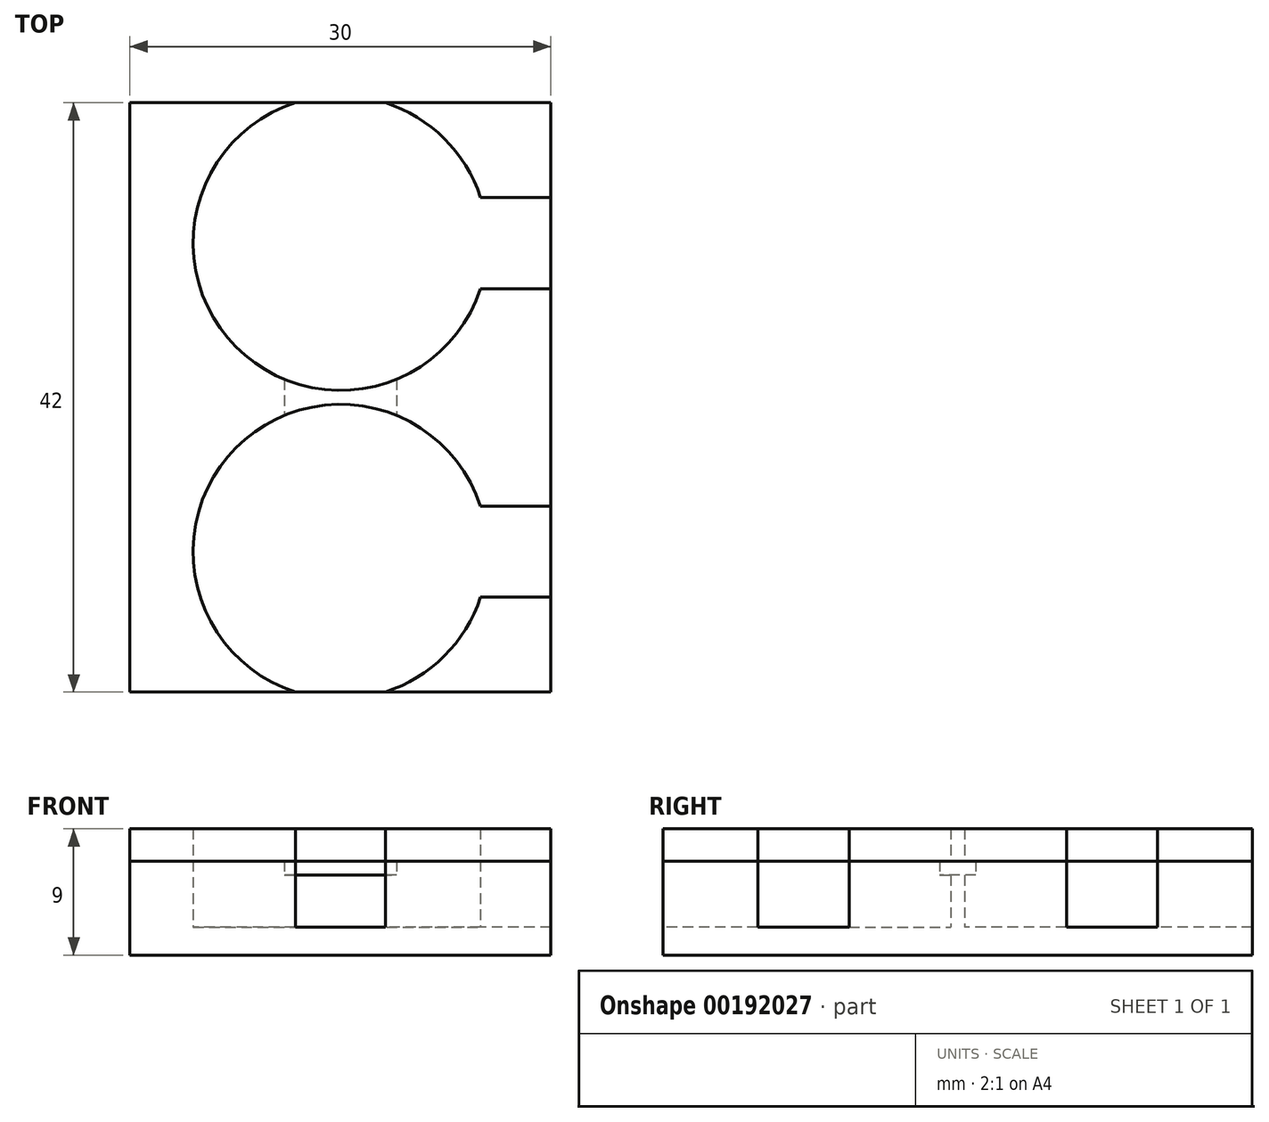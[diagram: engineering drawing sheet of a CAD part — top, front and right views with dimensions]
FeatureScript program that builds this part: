
annotation { "Feature Type Name" : "Feature", "Feature Type Description" : "" }
export const myFeature = defineFeature(function(context is Context, id is Id, definition is map)
    precondition{}
    {
        {
            var Q0;
            Q0=qCreatedBy(makeId("Top.planeOp"),FACE);
            var sketch = newSketch(context, id + "F0", { "sketchPlane" : qUnion([Q0])});
            skLineSegment(sketch, "E0.bottom", {"start": v(-15, 21) * mm, "end": v(15, 21) * mm});
            skLineSegment(sketch, "E0.top", {"start": v(-15, -21) * mm, "end": v(15, -21) * mm});
            skLineSegment(sketch, "E0.left", {"start": v(-15, 21) * mm, "end": v(-15, -21) * mm});
            skLineSegment(sketch, "E0.right", {"start": v(15, 21) * mm, "end": v(15, -21) * mm});
            skPoint(sketch, "E0.middle", {"position": v(0, 0) * mm});
            skSolve(sketch);
        }
        {
            var Q0;
            Q0=makeQuery(id+"F0.imprint","IMPRINT",FACE,{"disambiguationData":[TD([[makeQuery(id+"F0.imprint","IMPRINT",EDGE,{"derivedFrom":sQuery(id+"F0.wireOp",EDGE,"E0.bottom")}),-1.0]])]});
            var sketch = newSketch(context, id + "F1", { "sketchPlane" : qUnion([Q0])});
            skCircle(sketch, "E1", {"center": v(0, 11) * mm, "radius": 10.5 * mm});
            skSolve(sketch);
        }
        {
            var Q0;
            Q0=makeQuery(id+"F1.imprint","IMPRINT",FACE,{"disambiguationData":[TD([[makeQuery(id+"F1.imprint","IMPRINT",EDGE,{"derivedFrom":sQuery(id+"F1.wireOp",EDGE,"E1")}),-1.0]])]});
            var sketch = newSketch(context, id + "F2", { "sketchPlane" : qUnion([Q0])});
            skCircle(sketch, "E2", {"center": v(0, -11) * mm, "radius": 10.5 * mm});
            skSolve(sketch);
        }
        {
            var Q0;
            Q0=makeQuery(id+"F0.imprint","IMPRINT",FACE,{"disambiguationData":[TD([[makeQuery(id+"F0.imprint","IMPRINT",EDGE,{"derivedFrom":sQuery(id+"F0.wireOp",EDGE,"E0.bottom")}),-1.0]])]});
            extrude(context, id + "F3", {"entities" : qUnion([Q0]), "oppositeDirection" : true, "depth" : 2 * mm});
        }
        {
            var Q0;
            Q0=makeQuery(id+"F2.imprint","IMPRINT",FACE,{"disambiguationData":[TD([[makeQuery(id+"F2.imprint","IMPRINT",EDGE,{"derivedFrom":sQuery(id+"F2.wireOp",EDGE,"E2")}),-1.0]])]});
            var sketch = newSketch(context, id + "F4", { "sketchPlane" : qUnion([Q0])});
            skLineSegment(sketch, "E3.bottom", {"start": v(-0.01, -14.25) * mm, "end": v(17.7, -14.25) * mm});
            skLineSegment(sketch, "E3.top", {"start": v(-0.01, -7.75) * mm, "end": v(17.7, -7.75) * mm});
            skLineSegment(sketch, "E3.left", {"start": v(-0.01, -14.25) * mm, "end": v(-0.01, -7.75) * mm});
            skLineSegment(sketch, "E3.right", {"start": v(17.7, -14.25) * mm, "end": v(17.7, -7.75) * mm});
            skPoint(sketch, "E3.middle", {"position": v(0.75, 0) * mm});
            skSolve(sketch);
        }
        {
            var Q0;
            Q0=makeQuery(id+"F2.imprint","IMPRINT",FACE,{"disambiguationData":[TD([[makeQuery(id+"F2.imprint","IMPRINT",EDGE,{"derivedFrom":sQuery(id+"F2.wireOp",EDGE,"E2")}),-1.0]])]});
            var sketch = newSketch(context, id + "F5", { "sketchPlane" : qUnion([Q0])});
            skLineSegment(sketch, "E4.bottom", {"start": v(18, 14.25) * mm, "end": v(0, 14.25) * mm});
            skLineSegment(sketch, "E4.top", {"start": v(18, 7.75) * mm, "end": v(0, 7.75) * mm});
            skLineSegment(sketch, "E4.left", {"start": v(18, 14.25) * mm, "end": v(18, 7.75) * mm});
            skLineSegment(sketch, "E4.right", {"start": v(0, 14.25) * mm, "end": v(0, 7.75) * mm});
            skPoint(sketch, "E4.middle", {"position": v(0, 0) * mm});
            skSolve(sketch);
        }
        {
            var Q0;
            Q0 = qSketchRegion(id + "F0", true);
            extrude(context, id + "F6", {"entities" : qUnion([Q0]), "operationType" : NewBodyOperationType.ADD, "depth" : 4.7 * mm});
        }
        {
            var Q0;
            Q0=makeQuery(id+"F6.opExtrude","CAP_FACE",FACE,{"disambiguationData":[OSD([sQuery(id+"F0.wireOp",EDGE,"E0.bottom"),sQuery(id+"F0.wireOp",EDGE,"E0.top"),sQuery(id+"F0.wireOp",EDGE,"E0.left"),sQuery(id+"F0.wireOp",EDGE,"E0.right")])],"isStart":false});
            extrude(context, id + "F7", {"entities" : qUnion([Q0]), "depth" : 2.3 * mm});
        }
        {
            var Q0;
            Q0 = qSketchRegion(id + "F1", true);
            extrude(context, id + "F8", {"entities" : qUnion([Q0]), "operationType" : NewBodyOperationType.REMOVE, "depth" : 25 * mm});
        }
        {
            var Q0;
            Q0 = qSketchRegion(id + "F2", true);
            extrude(context, id + "F9", {"entities" : qUnion([Q0]), "operationType" : NewBodyOperationType.REMOVE, "depth" : 25 * mm});
        }
        {
            var Q0;
            Q0 = qSketchRegion(id + "F4", true);
            extrude(context, id + "F10", {"entities" : qUnion([Q0]), "operationType" : NewBodyOperationType.REMOVE, "depth" : 25 * mm});
        }
        {
            var Q0;
            Q0 = qSketchRegion(id + "F5", true);
            extrude(context, id + "F11", {"entities" : qUnion([Q0]), "operationType" : NewBodyOperationType.REMOVE, "depth" : 25 * mm});
        }
        {
            var Q0;
            Q0=makeQuery(id+"F6.opExtrude","CAP_FACE",FACE,{"disambiguationData":[OSD([sQuery(id+"F0.wireOp",EDGE,"E0.bottom"),sQuery(id+"F0.wireOp",EDGE,"E0.top"),sQuery(id+"F0.wireOp",EDGE,"E0.left"),sQuery(id+"F0.wireOp",EDGE,"E0.right")])],"isStart":false});
            var sketch = newSketch(context, id + "F12", { "sketchPlane" : qUnion([Q0])});
            skLineSegment(sketch, "E5.bottom", {"start": v(4, 5.71) * mm, "end": v(-4, 5.71) * mm});
            skLineSegment(sketch, "E5.top", {"start": v(4, -5.71) * mm, "end": v(-4, -5.71) * mm});
            skLineSegment(sketch, "E5.left", {"start": v(4, 5.71) * mm, "end": v(4, -5.71) * mm});
            skLineSegment(sketch, "E5.right", {"start": v(-4, 5.71) * mm, "end": v(-4, -5.71) * mm});
            skPoint(sketch, "E5.middle", {"position": v(0, 0) * mm});
            skSolve(sketch);
        }
        {
            var Q0;
            Q0 = qSketchRegion(id + "F12", true);
            extrude(context, id + "F13", {"entities" : qUnion([Q0]), "operationType" : NewBodyOperationType.REMOVE, "oppositeDirection" : true, "depth" : 1 * mm});
        }
    });
